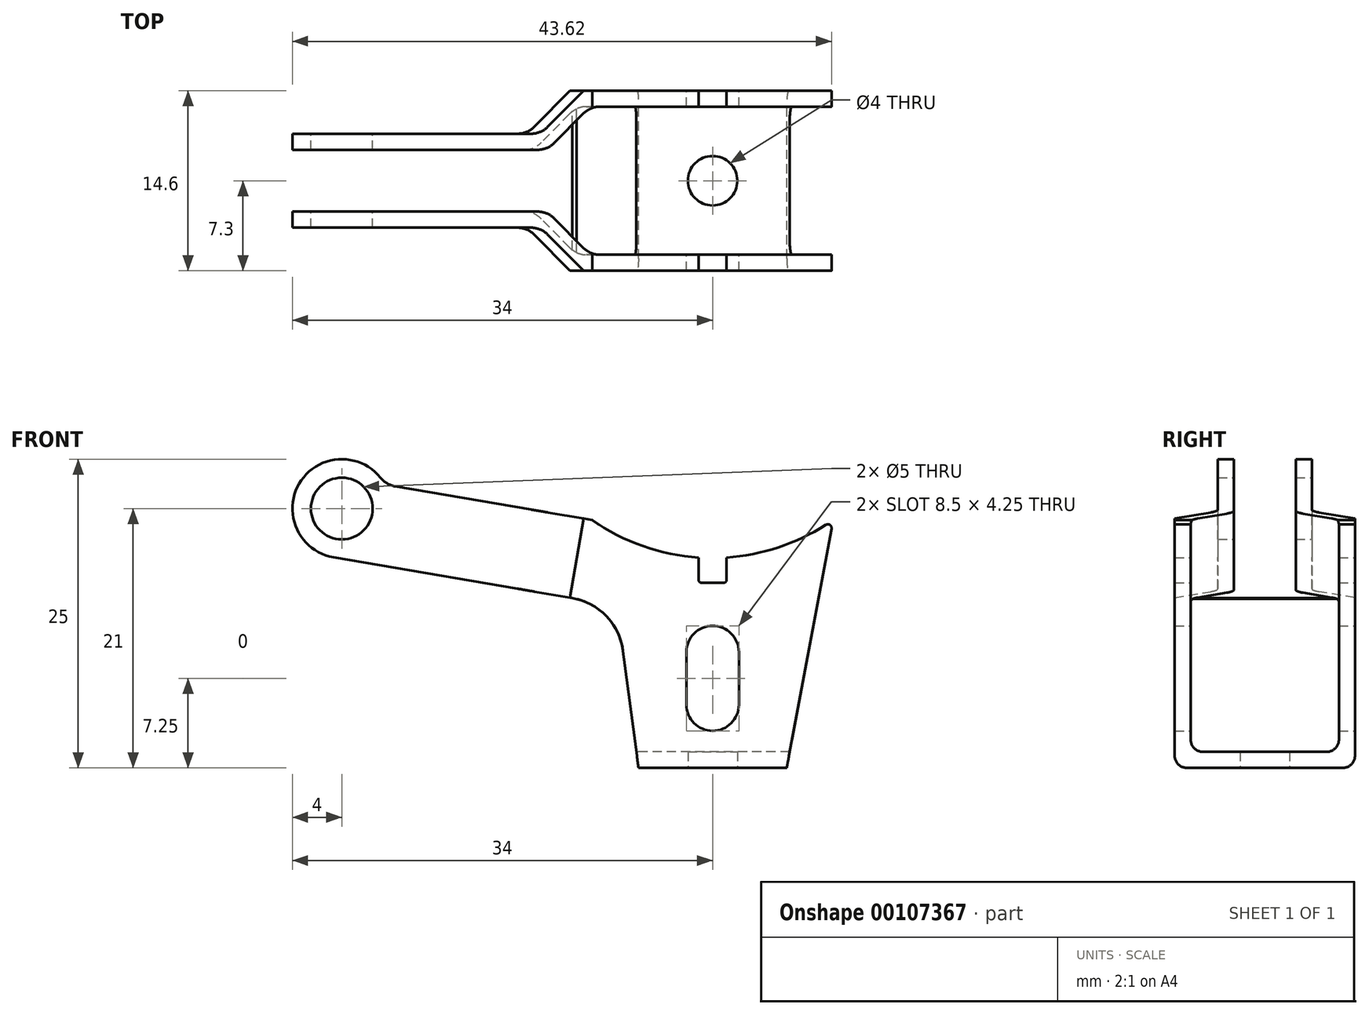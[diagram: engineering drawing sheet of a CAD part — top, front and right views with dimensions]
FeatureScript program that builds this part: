
annotation { "Feature Type Name" : "Feature", "Feature Type Description" : "" }
export const myFeature = defineFeature(function(context is Context, id is Id, definition is map)
    precondition{}
    {
        {
            var Q0;
            Q0=qCreatedBy(makeId("Front.planeOp"),FACE);
            var sketch = newSketch(context, id + "F0", { "sketchPlane" : qUnion([Q0])});
            skLineSegment(sketch, "E0", {"start": v(-6, 0) * mm, "end": v(6, 0) * mm});
            skLineSegment(sketch, "E1", {"start": v(6, 0) * mm, "end": v(9.62, 19.37) * mm});
            skLineSegment(sketch, "E2", {"start": v(-6, 0) * mm, "end": v(-7.25, 9.48) * mm});
            skArc(sketch, "E3", {"start": v(-9.75, 20.07) * mm, "mid": v(-0.35, 17) * mm, "end": v(9.16, 19.68) * mm});
            skLineSegment(sketch, "E4", {"start": v(0, 0) * mm, "end": v(0, 17) * mm, "construction": true});
            skLineSegment(sketch, "E5", {"start": v(-9.75, 20.07) * mm, "end": v(-25.67, 22.8) * mm});
            skArc(sketch, "E6", {"start": v(-26.89, 23.51) * mm, "mid": v(-33.45, 23.02) * mm, "end": v(-30.67, 17.06) * mm});
            skLineSegment(sketch, "E7", {"start": v(-30.67, 17.06) * mm, "end": v(-11.36, 13.76) * mm});
            skPoint(sketch, "E8.visualSharp", {"position": v(9.75, 20.07) * mm});
            skArc(sketch, "E8.filletArc", {"start": v(9.62, 19.37) * mm, "mid": v(9.5, 19.68) * mm, "end": v(9.16, 19.68) * mm});
            skPoint(sketch, "E9.visualSharp", {"position": v(-7.73, 13.13) * mm});
            skArc(sketch, "E9.filletArc", {"start": v(-7.25, 9.48) * mm, "mid": v(-8.6, 12.3) * mm, "end": v(-11.36, 13.76) * mm});
            skPoint(sketch, "E10.visualSharp", {"position": v(-26.5, 22.94) * mm});
            skArc(sketch, "E10.filletArc", {"start": v(-26.89, 23.51) * mm, "mid": v(-26.34, 23.04) * mm, "end": v(-25.67, 22.8) * mm});
            skLineSegment(sketch, "E11", {"start": v(9.75, 20.07) * mm, "end": v(0, 34) * mm});
            skLineSegment(sketch, "E12", {"start": v(-9.75, 20.07) * mm, "end": v(0, 34) * mm});
            skSolve(sketch);
        }
        {
            var Q0;
            Q0=makeQuery(id+"F0.imprint","IMPRINT",FACE,{"disambiguationData":[TD([[makeQuery(id+"F0.imprint","IMPRINT",EDGE,{"derivedFrom":sQuery(id+"F0.wireOp",EDGE,"E0")}),1.0]])]});
            extrude(context, id + "F1", {"entities" : qUnion([Q0]), "depth" : 7.3 * mm, "hasSecondDirection" : true, "secondDirectionOppositeDirection" : true, "secondDirectionDepth" : 7.3 * mm});
        }
        {
            var Q0;
            Q0=qCreatedBy(makeId("Front.planeOp"),FACE);
            var sketch = newSketch(context, id + "F2", { "sketchPlane" : qUnion([Q0])});
            skLineSegment(sketch, "E13", {"start": v(15, 78.04) * mm, "end": v(15, 1.3) * mm});
            skLineSegment(sketch, "E14", {"start": v(15, 1.3) * mm, "end": v(-11, 1.3) * mm});
            skLineSegment(sketch, "E15", {"start": v(0, 78.04) * mm, "end": v(15, 78.04) * mm});
            skLineSegment(sketch, "E16", {"start": v(-11, 1.3) * mm, "end": v(-11, 13.7) * mm});
            skLineSegment(sketch, "E17", {"start": v(-11, 13.7) * mm, "end": v(0, 78.04) * mm});
            skSolve(sketch);
        }
        {
            var Q0;
            Q0=makeQuery(id+"F2.imprint","IMPRINT",FACE,{"disambiguationData":[TD([[makeQuery(id+"F2.imprint","IMPRINT",EDGE,{"derivedFrom":sQuery(id+"F2.wireOp",EDGE,"E13")}),-1.0]])]});
            extrude(context, id + "F3", {"entities" : qUnion([Q0]), "operationType" : NewBodyOperationType.REMOVE, "depth" : 6 * mm, "hasSecondDirection" : true, "secondDirectionOppositeDirection" : true, "secondDirectionDepth" : 6 * mm});
        }
        {
            var Q0;
            Q0=qCreatedBy(makeId("Front.planeOp"),FACE);
            var sketch = newSketch(context, id + "F4", { "sketchPlane" : qUnion([Q0])});
            skLineSegment(sketch, "E18", {"start": v(-2.12, 9.38) * mm, "end": v(-2.12, 5.12) * mm});
            skArc(sketch, "E19", {"start": v(0, 11.5) * mm, "mid": v(-1.5, 10.88) * mm, "end": v(-2.13, 9.38) * mm});
            skArc(sketch, "E20", {"start": v(-2.12, 5.12) * mm, "mid": v(-1.5, 3.62) * mm, "end": v(0, 3) * mm});
            skArc(sketch, "E21.MirrorCS", {"start": v(0, 11.5) * mm, "mid": v(1.5, 10.88) * mm, "end": v(2.13, 9.38) * mm});
            skLineSegment(sketch, "E22.MirrorCS", {"start": v(2.12, 9.38) * mm, "end": v(2.12, 5.12) * mm});
            skArc(sketch, "E23.MirrorCS", {"start": v(2.12, 5.12) * mm, "mid": v(1.5, 3.62) * mm, "end": v(0, 3) * mm});
            skLineSegment(sketch, "E24", {"start": v(-1.12, 18) * mm, "end": v(-1.12, 15.2) * mm});
            skLineSegment(sketch, "E25", {"start": v(-0.92, 15) * mm, "end": v(0, 15) * mm});
            skLineSegment(sketch, "E26", {"start": v(0, 18) * mm, "end": v(-1.12, 18) * mm});
            skLineSegment(sketch, "E27.MirrorCS", {"start": v(0, 18) * mm, "end": v(1.12, 18) * mm});
            skLineSegment(sketch, "E28.MirrorCS", {"start": v(1.12, 18) * mm, "end": v(1.12, 15.2) * mm});
            skLineSegment(sketch, "E29.MirrorCS", {"start": v(0.93, 15) * mm, "end": v(0, 15) * mm});
            skPoint(sketch, "E30.visualSharp", {"position": v(-1.12, 15) * mm});
            skArc(sketch, "E30.filletArc", {"start": v(-1.12, 15.2) * mm, "mid": v(-1.07, 15.06) * mm, "end": v(-0.92, 15) * mm});
            skPoint(sketch, "E31.visualSharp", {"position": v(1.12, 15) * mm});
            skArc(sketch, "E31.filletArc", {"start": v(0.93, 15) * mm, "mid": v(1.07, 15.06) * mm, "end": v(1.12, 15.2) * mm});
            skSolve(sketch);
        }
        {
            var Q0;
            Q0=makeQuery(id+"F4.imprint","IMPRINT",FACE,{"disambiguationData":[TD([[makeQuery(id+"F4.imprint","IMPRINT",EDGE,{"derivedFrom":sQuery(id+"F4.wireOp",EDGE,"E24")}),1.0]])]});
            var Q1;
            Q1=makeQuery(id+"F4.imprint","IMPRINT",FACE,{"disambiguationData":[TD([[makeQuery(id+"F4.imprint","IMPRINT",EDGE,{"derivedFrom":sQuery(id+"F4.wireOp",EDGE,"E18")}),1.0]])]});
            extrude(context, id + "F5", {"entities" : qUnion([Q0, Q1]), "operationType" : NewBodyOperationType.REMOVE, "depth" : 10 * mm, "hasSecondDirection" : true, "secondDirectionOppositeDirection" : true, "secondDirectionDepth" : 10 * mm});
        }
        {
            var Q0;
            Q0=makeQuery(id+"F1.opExtrude","SWEPT_FACE",FACE,{"disambiguationData":[OSD([sQuery(id+"F0.wireOp",EDGE,"E7")])]});
            cPlane(context, id + "F6", {"entities" : qUnion([Q0]), "cplaneType" : CPlaneType.OFFSET, "offset" : 0 * mm, "width" : 150 * mm, "height" : 150 * mm});
        }
        {
            var Q0;
            Q0=qCreatedBy(id+"F6.planeOp",FACE);
            var sketch = newSketch(context, id + "F7", { "sketchPlane" : qUnion([Q0])});
            skLineSegment(sketch, "E32", {"start": v(-13.69, -7.3) * mm, "end": v(-17.19, -3.8) * mm});
            skLineSegment(sketch, "E33", {"start": v(-17.19, -3.8) * mm, "end": v(-42, -3.8) * mm});
            skLineSegment(sketch, "E34", {"start": v(-42, -3.8) * mm, "end": v(-42, -7.3) * mm});
            skLineSegment(sketch, "E35", {"start": v(-42, -7.3) * mm, "end": v(-13.69, -7.3) * mm});
            skLineSegment(sketch, "E36.MirrorCS", {"start": v(-42, 3.8) * mm, "end": v(-42, 7.3) * mm});
            skLineSegment(sketch, "E37.MirrorCS", {"start": v(-42, 7.3) * mm, "end": v(-13.69, 7.3) * mm});
            skLineSegment(sketch, "E38.MirrorCS", {"start": v(-13.69, 7.3) * mm, "end": v(-17.19, 3.8) * mm});
            skLineSegment(sketch, "E39.MirrorCS", {"start": v(-17.19, 3.8) * mm, "end": v(-42, 3.8) * mm});
            skLineSegment(sketch, "E40", {"start": v(-13.15, -6) * mm, "end": v(-16.65, -2.5) * mm});
            skLineSegment(sketch, "E41", {"start": v(-16.65, -2.5) * mm, "end": v(-42, -2.5) * mm});
            skLineSegment(sketch, "E42", {"start": v(-42, -2.5) * mm, "end": v(-42, 0) * mm});
            skLineSegment(sketch, "E43", {"start": v(-13.15, -6) * mm, "end": v(-13.15, 0) * mm});
            skLineSegment(sketch, "E44.MirrorCS", {"start": v(-13.15, 6) * mm, "end": v(-13.15, 0) * mm});
            skLineSegment(sketch, "E45.MirrorCS", {"start": v(-13.15, 6) * mm, "end": v(-16.65, 2.5) * mm});
            skLineSegment(sketch, "E46.MirrorCS", {"start": v(-16.65, 2.5) * mm, "end": v(-42, 2.5) * mm});
            skLineSegment(sketch, "E47.MirrorCS", {"start": v(-42, 2.5) * mm, "end": v(-42, 0) * mm});
            skSolve(sketch);
        }
        {
            var Q0;
            Q0=qSketchRegion(id+"F7",true);
            extrude(context, id + "F8", {"entities" : qUnion([Q0]), "operationType" : NewBodyOperationType.REMOVE, "oppositeDirection" : true, "depth" : 25 * mm});
        }
        {
            var Q0;
            Q0=qCreatedBy(makeId("Front.planeOp"),FACE);
            var sketch = newSketch(context, id + "F9", { "sketchPlane" : qUnion([Q0])});
            skCircle(sketch, "E48", {"center": v(-30, 21) * mm, "radius": 2.5 * mm});
            skSolve(sketch);
        }
        {
            var Q0;
            Q0=makeQuery(id+"F9.imprint","IMPRINT",FACE,{"disambiguationData":[TD([[makeQuery(id+"F9.imprint","IMPRINT",EDGE,{"derivedFrom":sQuery(id+"F9.wireOp",EDGE,"E48")}),1.0]])]});
            extrude(context, id + "F10", {"entities" : qUnion([Q0]), "operationType" : NewBodyOperationType.REMOVE, "depth" : 10 * mm, "hasSecondDirection" : true, "secondDirectionOppositeDirection" : true, "secondDirectionDepth" : 10 * mm});
        }
        {
            var Q0;
            Q0=makeQuery(id+"F8.boolean.opBoolean","COPY",EDGE,{"derivedFrom":makeQuery(id+"F8.opExtrude","SWEPT_EDGE",EDGE,{"disambiguationData":[OSD([sQuery(id+"F7.wireOp",EDGE,"E32"),sQuery(id+"F7.wireOp",EDGE,"E33")])]})});
            var Q1;
            Q1=makeQuery(id+"F8.boolean.opBoolean","COPY",EDGE,{"derivedFrom":makeQuery(id+"F8.opExtrude","SWEPT_EDGE",EDGE,{"disambiguationData":[OSD([sQuery(id+"F7.wireOp",EDGE,"E32"),sQuery(id+"F7.wireOp",EDGE,"E35")])]})});
            var Q2;
            Q2=makeQuery(id+"F8.boolean.opBoolean","COPY",EDGE,{"derivedFrom":makeQuery(id+"F8.opExtrude","SWEPT_EDGE",EDGE,{"disambiguationData":[OSD([sQuery(id+"F7.wireOp",EDGE,"E45.MirrorCS"),sQuery(id+"F7.wireOp",EDGE,"E46.MirrorCS")])]})});
            var Q3;
            Q3=makeQuery(id+"F8.boolean.opBoolean","MERGE",EDGE,{"derivedFrom":[makeQuery(id+"F3.boolean.opBoolean","COPY",EDGE,{"derivedFrom":makeQuery(id+"F3.opExtrude","CAP_EDGE",EDGE,{"disambiguationData":[OSD([sQuery(id+"F2.wireOp",EDGE,"E17")])],"isStart":false})}),makeQuery(id+"F8.opExtrude","SWEPT_EDGE",EDGE,{"disambiguationData":[OSD([sQuery(id+"F7.wireOp",EDGE,"E44.MirrorCS"),sQuery(id+"F7.wireOp",EDGE,"E45.MirrorCS")])]})]});
            var Q4;
            Q4=makeQuery(id+"F8.boolean.opBoolean","COPY",EDGE,{"derivedFrom":makeQuery(id+"F8.opExtrude","SWEPT_EDGE",EDGE,{"disambiguationData":[OSD([sQuery(id+"F7.wireOp",EDGE,"E37.MirrorCS"),sQuery(id+"F7.wireOp",EDGE,"E38.MirrorCS")])]})});
            var Q5;
            Q5=makeQuery(id+"F8.boolean.opBoolean","COPY",EDGE,{"derivedFrom":makeQuery(id+"F8.opExtrude","SWEPT_EDGE",EDGE,{"disambiguationData":[OSD([sQuery(id+"F7.wireOp",EDGE,"E38.MirrorCS"),sQuery(id+"F7.wireOp",EDGE,"E39.MirrorCS")])]})});
            var Q6;
            Q6=makeQuery(id+"F8.boolean.opBoolean","COPY",EDGE,{"derivedFrom":makeQuery(id+"F8.opExtrude","SWEPT_EDGE",EDGE,{"disambiguationData":[OSD([sQuery(id+"F7.wireOp",EDGE,"E40"),sQuery(id+"F7.wireOp",EDGE,"E41")])]})});
            var Q7;
            Q7=makeQuery(id+"F8.boolean.opBoolean","MERGE",EDGE,{"derivedFrom":[makeQuery(id+"F3.boolean.opBoolean","COPY",EDGE,{"derivedFrom":makeQuery(id+"F3.opExtrude","CAP_EDGE",EDGE,{"disambiguationData":[OSD([sQuery(id+"F2.wireOp",EDGE,"E17")])],"isStart":true})}),makeQuery(id+"F8.opExtrude","SWEPT_EDGE",EDGE,{"disambiguationData":[OSD([sQuery(id+"F7.wireOp",EDGE,"E40"),sQuery(id+"F7.wireOp",EDGE,"E43")])]})]});
            fillet(context, id + "F11", {"entities" : qUnion([Q0, Q1, Q2, Q3, Q4, Q5, Q6, Q7]), "radius" : 2 * mm, "tangentPropagation" : true, "allowEdgeOverflow" : false});
        }
        {
            var Q0;
            Q0=makeQuery(id+"F3.boolean.opBoolean","COPY",EDGE,{"derivedFrom":makeQuery(id+"F3.opExtrude","CAP_EDGE",EDGE,{"disambiguationData":[OSD([sQuery(id+"F2.wireOp",EDGE,"E14")])],"isStart":true})});
            var Q1;
            Q1=makeQuery(id+"F1.opExtrude","CAP_EDGE",EDGE,{"disambiguationData":[OSD([sQuery(id+"F0.wireOp",EDGE,"E0")])],"isStart":false});
            var Q2;
            Q2=makeQuery(id+"F3.boolean.opBoolean","COPY",EDGE,{"derivedFrom":makeQuery(id+"F3.opExtrude","CAP_EDGE",EDGE,{"disambiguationData":[OSD([sQuery(id+"F2.wireOp",EDGE,"E14")])],"isStart":false})});
            var Q3;
            Q3=makeQuery(id+"F1.opExtrude","CAP_EDGE",EDGE,{"disambiguationData":[OSD([sQuery(id+"F0.wireOp",EDGE,"E0")])],"isStart":true});
            fillet(context, id + "F12", {"entities" : qUnion([Q0, Q1, Q2, Q3]), "radius" : 1 * mm, "tangentPropagation" : true, "allowEdgeOverflow" : false});
        }
        {
            var Q0;
            Q0=qCreatedBy(makeId("Top.planeOp"),FACE);
            var sketch = newSketch(context, id + "F13", { "sketchPlane" : qUnion([Q0])});
            skCircle(sketch, "E49", {"center": v(0, 0) * mm, "radius": 2 * mm});
            skSolve(sketch);
        }
        {
            var Q0;
            Q0=qSketchRegion(id+"F13",true);
            extrude(context, id + "F14", {"entities" : qUnion([Q0]), "operationType" : NewBodyOperationType.REMOVE, "depth" : 5 * mm});
        }
    });
